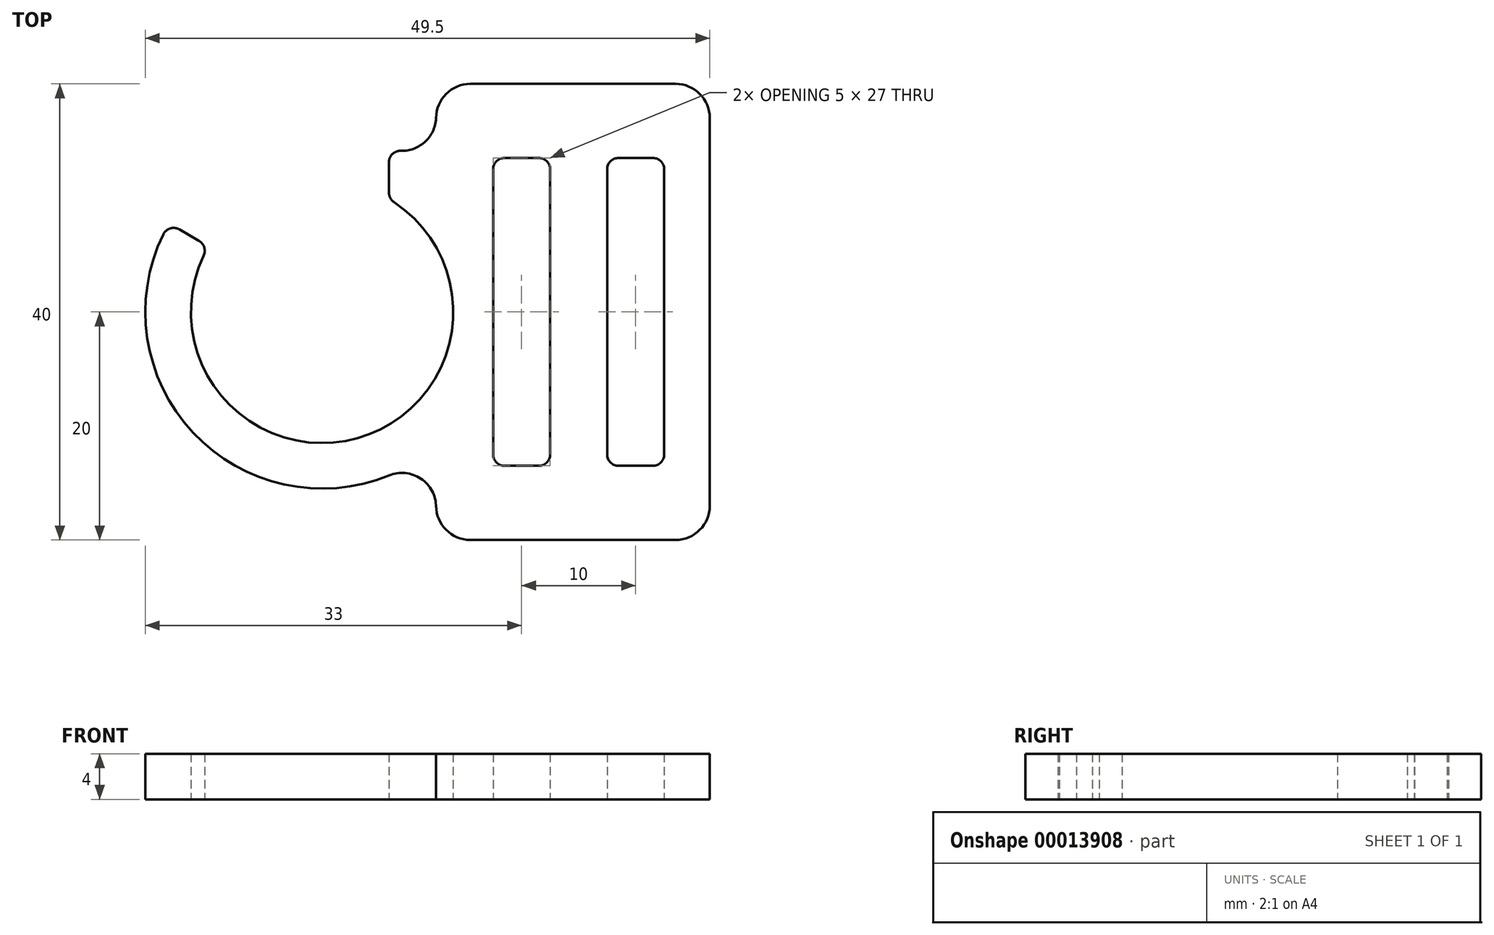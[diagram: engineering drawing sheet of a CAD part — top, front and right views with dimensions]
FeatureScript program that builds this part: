
annotation { "Feature Type Name" : "Feature", "Feature Type Description" : "" }
export const myFeature = defineFeature(function(context is Context, id is Id, definition is map)
    precondition{}
    {
        {
            var Q0;
            Q0=qCreatedBy(makeId("Top.planeOp"),FACE);
            var sketch = newSketch(context, id + "F0", { "sketchPlane" : qUnion([Q0])});
            skArc(sketch, "E0", {"start": v(-13.93, 6.8) * mm, "mid": v(-11.32, -10.59) * mm, "end": v(5.86, -14.35) * mm});
            skLineSegment(sketch, "E1.bottom", {"start": v(13, 20) * mm, "end": v(31, 20) * mm});
            skLineSegment(sketch, "E1.top", {"start": v(13, -20) * mm, "end": v(31, -20) * mm});
            skLineSegment(sketch, "E1.left", {"start": v(10, 17.12) * mm, "end": v(10, 17) * mm});
            skLineSegment(sketch, "E1.right", {"start": v(34, 17) * mm, "end": v(34, -17) * mm});
            skArc(sketch, "E2", {"start": v(-10.39, 4.93) * mm, "mid": v(3.1, -11.07) * mm, "end": v(6.32, 9.61) * mm});
            skLineSegment(sketch, "E3.trimOffspring", {"start": v(10, -17) * mm, "end": v(10, -17.12) * mm});
            skLineSegment(sketch, "E4.bottom", {"start": v(16, 13.5) * mm, "end": v(19, 13.5) * mm});
            skLineSegment(sketch, "E4.top", {"start": v(16, -13.5) * mm, "end": v(19, -13.5) * mm});
            skLineSegment(sketch, "E4.left", {"start": v(15, 12.5) * mm, "end": v(15, -12.5) * mm});
            skLineSegment(sketch, "E4.right", {"start": v(20, 12.5) * mm, "end": v(20, -12.5) * mm});
            skLineSegment(sketch, "E5.bottom", {"start": v(26, 13.5) * mm, "end": v(29, 13.5) * mm});
            skLineSegment(sketch, "E5.top", {"start": v(26, -13.5) * mm, "end": v(29, -13.5) * mm});
            skLineSegment(sketch, "E5.left", {"start": v(25, 12.5) * mm, "end": v(25, -12.5) * mm});
            skLineSegment(sketch, "E5.right", {"start": v(30, 12.5) * mm, "end": v(30, -12.5) * mm});
            skLineSegment(sketch, "E6", {"start": v(0, 0) * mm, "end": v(34, 0) * mm, "construction": true});
            skPoint(sketch, "E7", {"position": v(25, 0) * mm});
            skPoint(sketch, "E8.visualSharp", {"position": v(10, 11.84) * mm});
            skArc(sketch, "E8.filletArc", {"start": v(6.9, 14.13) * mm, "mid": v(9.09, 14.97) * mm, "end": v(10, 17.12) * mm});
            skPoint(sketch, "E9.visualSharp", {"position": v(10, -11.84) * mm});
            skArc(sketch, "E9.filletArc", {"start": v(10, -17.12) * mm, "mid": v(8.67, -14.63) * mm, "end": v(5.86, -14.35) * mm});
            skPoint(sketch, "E10.visualSharp", {"position": v(10, -20) * mm});
            skArc(sketch, "E10.filletArc", {"start": v(10, -17) * mm, "mid": v(10.88, -19.12) * mm, "end": v(13, -20) * mm});
            skPoint(sketch, "E11.visualSharp", {"position": v(34, -20) * mm});
            skArc(sketch, "E11.filletArc", {"start": v(31, -20) * mm, "mid": v(33.12, -19.12) * mm, "end": v(34, -17) * mm});
            skPoint(sketch, "E12.visualSharp", {"position": v(34, 20) * mm});
            skArc(sketch, "E12.filletArc", {"start": v(34, 17) * mm, "mid": v(33.12, 19.12) * mm, "end": v(31, 20) * mm});
            skPoint(sketch, "E13.visualSharp", {"position": v(10, 20) * mm});
            skArc(sketch, "E13.filletArc", {"start": v(13, 20) * mm, "mid": v(10.88, 19.12) * mm, "end": v(10, 17) * mm});
            skPoint(sketch, "E14.visualSharp", {"position": v(15, 13.5) * mm});
            skArc(sketch, "E14.filletArc", {"start": v(16, 13.5) * mm, "mid": v(15.3, 13.2) * mm, "end": v(15, 12.5) * mm});
            skPoint(sketch, "E15.visualSharp", {"position": v(20, 13.5) * mm});
            skArc(sketch, "E15.filletArc", {"start": v(20, 12.5) * mm, "mid": v(19.7, 13.2) * mm, "end": v(19, 13.5) * mm});
            skPoint(sketch, "E16.visualSharp", {"position": v(25, 13.5) * mm});
            skArc(sketch, "E16.filletArc", {"start": v(26, 13.5) * mm, "mid": v(25.3, 13.2) * mm, "end": v(25, 12.5) * mm});
            skPoint(sketch, "E17.visualSharp", {"position": v(30, 13.5) * mm});
            skArc(sketch, "E17.filletArc", {"start": v(30, 12.5) * mm, "mid": v(29.7, 13.2) * mm, "end": v(29, 13.5) * mm});
            skPoint(sketch, "E18.visualSharp", {"position": v(30, -13.5) * mm});
            skArc(sketch, "E18.filletArc", {"start": v(29, -13.5) * mm, "mid": v(29.7, -13.2) * mm, "end": v(30, -12.5) * mm});
            skPoint(sketch, "E19.visualSharp", {"position": v(25, -13.5) * mm});
            skArc(sketch, "E19.filletArc", {"start": v(25, -12.5) * mm, "mid": v(25.3, -13.2) * mm, "end": v(26, -13.5) * mm});
            skPoint(sketch, "E20.visualSharp", {"position": v(15, -13.5) * mm});
            skArc(sketch, "E20.filletArc", {"start": v(15, -12.5) * mm, "mid": v(15.3, -13.2) * mm, "end": v(16, -13.5) * mm});
            skPoint(sketch, "E21.visualSharp", {"position": v(20, -13.5) * mm});
            skArc(sketch, "E21.filletArc", {"start": v(19, -13.5) * mm, "mid": v(19.7, -13.2) * mm, "end": v(20, -12.5) * mm});
            skLineSegment(sketch, "E22", {"start": v(5.86, 13.13) * mm, "end": v(5.86, 10.45) * mm});
            skLineSegment(sketch, "E23", {"start": v(-12.53, 7.23) * mm, "end": v(-10.8, 6.23) * mm});
            skPoint(sketch, "E24.visualSharp", {"position": v(-13.42, 7.75) * mm});
            skArc(sketch, "E24.filletArc", {"start": v(-12.53, 7.23) * mm, "mid": v(-13.32, 7.32) * mm, "end": v(-13.93, 6.8) * mm});
            skPoint(sketch, "E25.visualSharp", {"position": v(-9.96, 5.75) * mm});
            skArc(sketch, "E25.filletArc", {"start": v(-10.39, 4.93) * mm, "mid": v(-10.34, 5.66) * mm, "end": v(-10.8, 6.23) * mm});
            skPoint(sketch, "E26.visualSharp", {"position": v(5.86, 9.9) * mm});
            skArc(sketch, "E26.filletArc", {"start": v(5.86, 10.45) * mm, "mid": v(5.98, 9.97) * mm, "end": v(6.32, 9.61) * mm});
            skPoint(sketch, "E27.visualSharp", {"position": v(5.86, 14.35) * mm});
            skArc(sketch, "E27.filletArc", {"start": v(6.9, 14.13) * mm, "mid": v(6.17, 13.85) * mm, "end": v(5.86, 13.13) * mm});
            skSolve(sketch);
        }
        {
            var Q0;
            Q0 = qSketchRegion(id + "F0", true);
            extrude(context, id + "F1", {"entities" : qUnion([Q0]), "depth" : 4 * mm});
        }
    });
